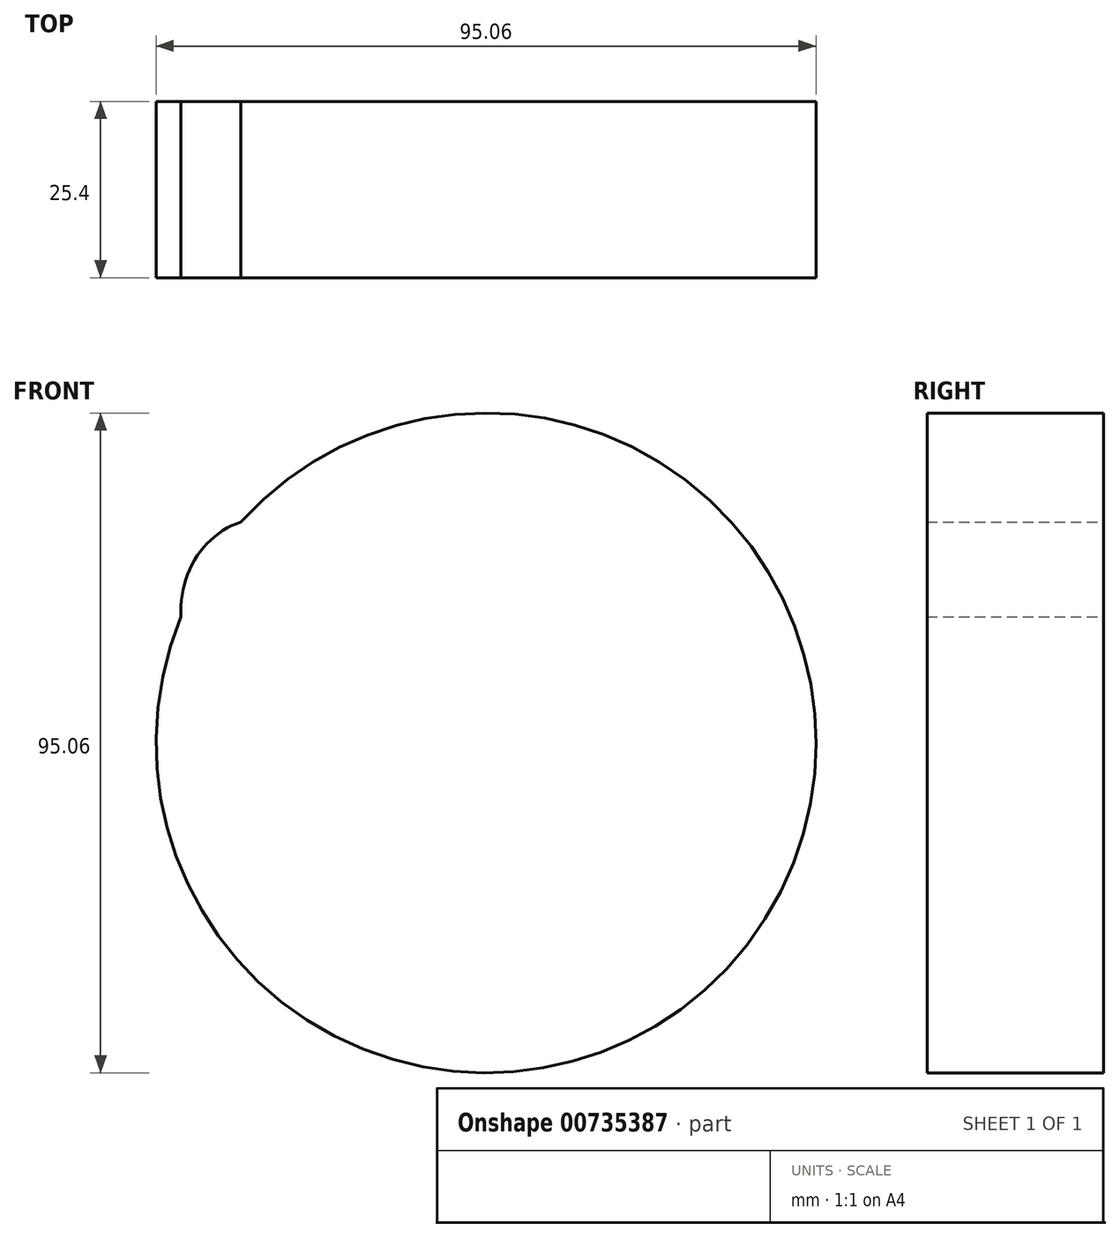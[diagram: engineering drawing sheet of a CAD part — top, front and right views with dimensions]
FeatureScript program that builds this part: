
annotation { "Feature Type Name" : "Feature", "Feature Type Description" : "" }
export const myFeature = defineFeature(function(context is Context, id is Id, definition is map)
    precondition{}
    {
        {
            var Q0;
            Q0=qCreatedBy(makeId("Front.planeOp"),FACE);
            var sketch = newSketch(context, id + "F0", { "sketchPlane" : qUnion([Q0])});
            skCircle(sketch, "E0", {"center": v(9.42, 23.6) * mm, "radius": 47.53 * mm});
            skEllipse(sketch, "E1", {"center": v(27.33, 43.14) * mm, "majorRadius": 19.72 * mm, "minorRadius": 12.3 * mm, "majorAxis": v(0.96, -0.3)});
            skEllipse(sketch, "E2", {"center": v(-22.44, 42.68) * mm, "majorRadius": 12.1 * mm, "minorRadius": 13.3 * mm, "majorAxis": v(1, 0)});
            skEllipse(sketch, "E3", {"center": v(-7.1, 11.98) * mm, "majorRadius": 24.42 * mm, "minorRadius": 19.77 * mm, "majorAxis": v(1, 0)});
            skSolve(sketch);
        }
        {
            var Q0;
            {var subQ0=sQuery(id+"F0.wireOp",EDGE,"E2");var subQ1=sQuery(id+"F0.wireOp",EDGE,"E0");var subQ2=makeQuery(id+"F0.imprint","INTERSECT",VERTEX,{"disambiguationData":[OD(0.0)],"derivedFrom":[subQ1,subQ0]});Q0=makeQuery(id+"F0.imprint","IMPRINT",FACE,{"disambiguationData":[TD([[makeQuery(id+"F0.imprint","IMPRINT",EDGE,{"disambiguationData":[TD([[subQ2,1.0]])],"derivedFrom":subQ1}),-1.0]])]});}
            var Q1;
            {var subQ0=sQuery(id+"F0.wireOp",EDGE,"E2");var subQ1=sQuery(id+"F0.wireOp",EDGE,"E0");var subQ2=makeQuery(id+"F0.imprint","INTERSECT",VERTEX,{"disambiguationData":[OD(0.0)],"derivedFrom":[subQ1,subQ0]});Q1=makeQuery(id+"F0.imprint","IMPRINT",FACE,{"disambiguationData":[TD([[makeQuery(id+"F0.imprint","IMPRINT",EDGE,{"disambiguationData":[TD([[subQ2,1.0]])],"derivedFrom":subQ1}),1.0]])]});}
            var Q2;
            Q2=makeQuery(id+"F0.imprint","IMPRINT",FACE,{"disambiguationData":[TD([[makeQuery(id+"F0.imprint","IMPRINT",EDGE,{"derivedFrom":sQuery(id+"F0.wireOp",EDGE,"E1")}),-1.0]])]});
            var Q3;
            Q3=makeQuery(id+"F0.imprint","IMPRINT",FACE,{"disambiguationData":[TD([[makeQuery(id+"F0.imprint","IMPRINT",EDGE,{"derivedFrom":sQuery(id+"F0.wireOp",EDGE,"E1")}),1.0]])]});
            var Q4;
            Q4=makeQuery(id+"F0.imprint","IMPRINT",FACE,{"disambiguationData":[TD([[makeQuery(id+"F0.imprint","IMPRINT",EDGE,{"derivedFrom":sQuery(id+"F0.wireOp",EDGE,"E3")}),1.0]])]});
            extrude(context, id + "F1", {"entities" : qUnion([Q0, Q1, Q2, Q3, Q4]), "depth" : 25.4 * mm, "offsetDistance" : 25.4 * mm});
        }
    });
